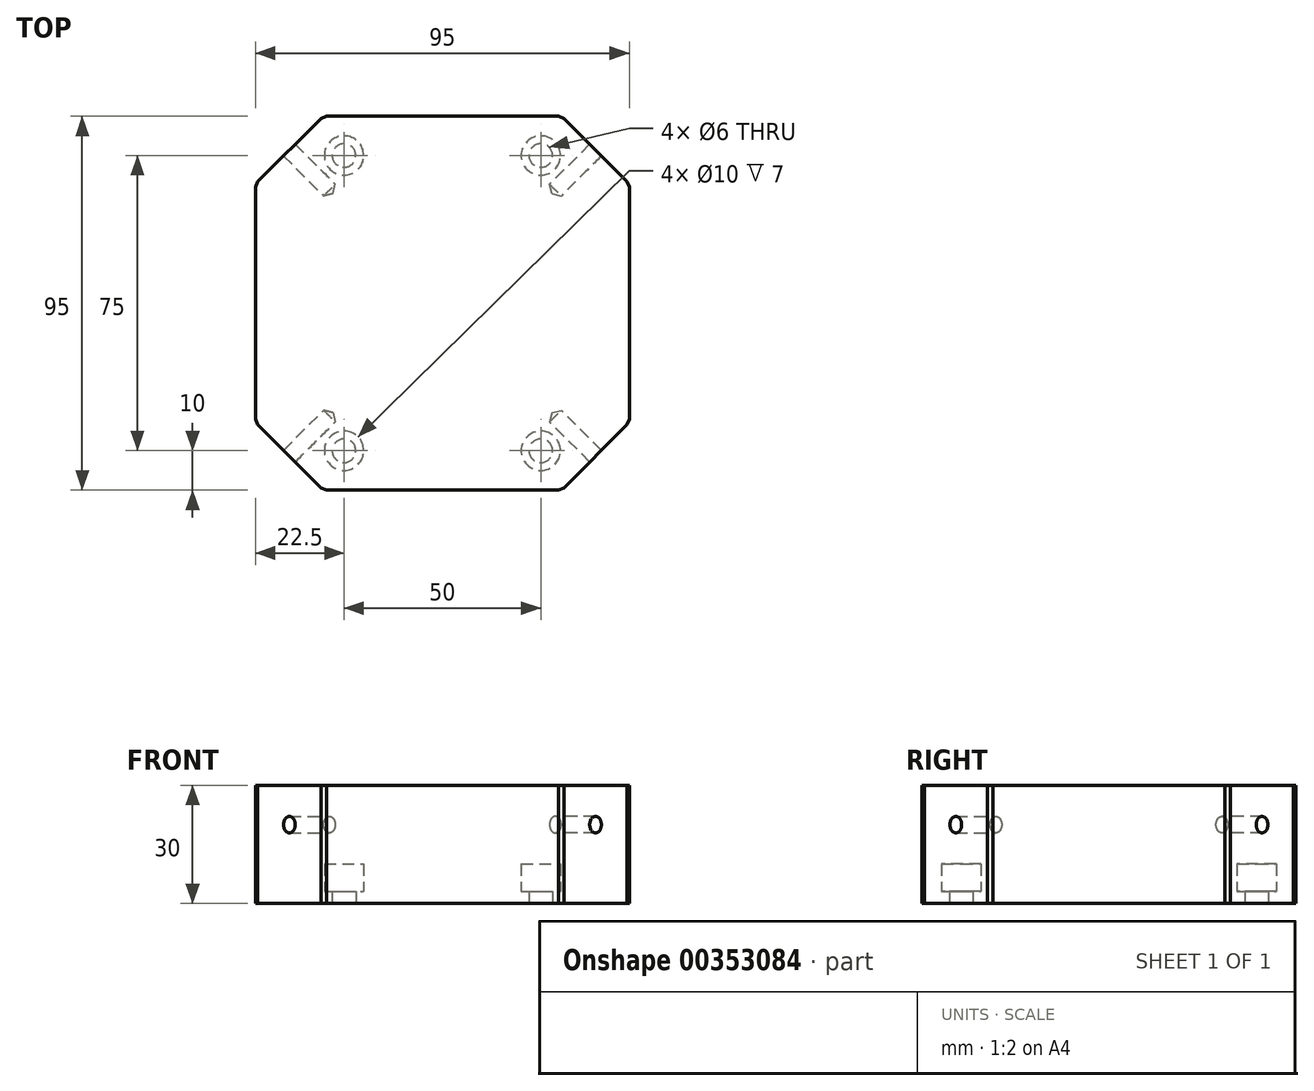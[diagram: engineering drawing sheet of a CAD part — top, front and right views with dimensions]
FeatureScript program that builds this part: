
annotation { "Feature Type Name" : "Feature", "Feature Type Description" : "" }
export const myFeature = defineFeature(function(context is Context, id is Id, definition is map)
    precondition{}
    {
        {
            var Q0;
            Q0=qCreatedBy(makeId("Top.planeOp"),FACE);
            var sketch = newSketch(context, id + "F0", { "sketchPlane" : qUnion([Q0])});
            skLineSegment(sketch, "E0.bottom", {"start": v(-47.5, 47.5) * mm, "end": v(47.5, 47.5) * mm});
            skLineSegment(sketch, "E0.top", {"start": v(-47.5, -47.5) * mm, "end": v(47.5, -47.5) * mm});
            skLineSegment(sketch, "E0.left", {"start": v(-47.5, 47.5) * mm, "end": v(-47.5, -47.5) * mm});
            skLineSegment(sketch, "E0.right", {"start": v(47.5, 47.5) * mm, "end": v(47.5, -47.5) * mm});
            skCircle(sketch, "E1", {"center": v(0, 0) * mm, "radius": 50.15 * mm});
            skPoint(sketch, "E2", {"position": v(-25, 37.5) * mm});
            skPoint(sketch, "E3.MirrorP", {"position": v(25, 37.5) * mm});
            skPoint(sketch, "E4.MirrorP", {"position": v(-25, -37.5) * mm});
            skPoint(sketch, "E5.MirrorP", {"position": v(25, -37.5) * mm});
            skLineSegment(sketch, "E6.bottom", {"start": v(77.78, 0) * mm, "end": v(0, -77.78) * mm});
            skLineSegment(sketch, "E6.top", {"start": v(0, 77.78) * mm, "end": v(-77.78, 0) * mm});
            skLineSegment(sketch, "E6.left", {"start": v(77.78, 0) * mm, "end": v(0, 77.78) * mm});
            skLineSegment(sketch, "E6.right", {"start": v(0, -77.78) * mm, "end": v(-77.78, 0) * mm});
            skSolve(sketch);
        }
        {
            var Q0;
            {var subQ0=sQuery(id+"F0.wireOp",EDGE,"E1");var subQ10=sQuery(id+"F0.wireOp",EDGE,"E0.bottom");var subQ11=makeQuery(id+"F0.imprint","INTERSECT",VERTEX,{"disambiguationData":[OD(0.0)],"derivedFrom":[subQ10,subQ0]});Q0=makeQuery(id+"F0.imprint","IMPRINT",FACE,{"disambiguationData":[TD([[makeQuery(id+"F0.imprint","IMPRINT",EDGE,{"disambiguationData":[TD([[subQ11,-1.0]])],"derivedFrom":subQ10}),-1.0]])]});}
            var Q1;
            {var subQ0=sQuery(id+"F0.wireOp",EDGE,"XF65z8Od-p8Gt-gOkY-70P6-u7OeU0bEHKry");var subQ1=sQuery(id+"F0.wireOp",EDGE,"E0.bottom");var subQ2=makeQuery(id+"F0.imprint","INTERSECT",VERTEX,{"disambiguationData":[OD(0.0)],"derivedFrom":[subQ1,subQ0]});Q1=makeQuery(id+"F0.imprint","IMPRINT",FACE,{"disambiguationData":[TD([[makeQuery(id+"F0.imprint","IMPRINT",EDGE,{"disambiguationData":[TD([[subQ2,-1.0]])],"derivedFrom":subQ1}),-1.0]])]});}
            var Q2;
            {var subQ0=sQuery(id+"F0.wireOp",EDGE,"XF65z8Od-p8Gt-gOkY-70P6-u7OeU0bEHKry");var subQ1=sQuery(id+"F0.wireOp",EDGE,"E0.top");var subQ2=makeQuery(id+"F0.imprint","INTERSECT",VERTEX,{"disambiguationData":[OD(0.0)],"derivedFrom":[subQ1,subQ0]});Q2=makeQuery(id+"F0.imprint","IMPRINT",FACE,{"disambiguationData":[TD([[makeQuery(id+"F0.imprint","IMPRINT",EDGE,{"disambiguationData":[TD([[subQ2,-1.0]])],"derivedFrom":subQ1}),1.0]])]});}
            var Q3;
            {var subQ0=sQuery(id+"F0.wireOp",EDGE,"XF65z8Od-p8Gt-gOkY-70P6-u7OeU0bEHKry");var subQ1=sQuery(id+"F0.wireOp",EDGE,"E0.top");var subQ2=makeQuery(id+"F0.imprint","INTERSECT",VERTEX,{"disambiguationData":[OD(1.0)],"derivedFrom":[subQ1,subQ0]});Q3=makeQuery(id+"F0.imprint","IMPRINT",FACE,{"disambiguationData":[TD([[makeQuery(id+"F0.imprint","IMPRINT",EDGE,{"disambiguationData":[TD([[subQ2,1.0]])],"derivedFrom":subQ1}),1.0]])]});}
            var Q4;
            {var subQ0=sQuery(id+"F0.wireOp",EDGE,"XF65z8Od-p8Gt-gOkY-70P6-u7OeU0bEHKry");var subQ1=sQuery(id+"F0.wireOp",EDGE,"E0.bottom");var subQ2=makeQuery(id+"F0.imprint","INTERSECT",VERTEX,{"disambiguationData":[OD(1.0)],"derivedFrom":[subQ1,subQ0]});Q4=makeQuery(id+"F0.imprint","IMPRINT",FACE,{"disambiguationData":[TD([[makeQuery(id+"F0.imprint","IMPRINT",EDGE,{"disambiguationData":[TD([[subQ2,1.0]])],"derivedFrom":subQ1}),-1.0]])]});}
            var Q5;
            {var subQ0=sQuery(id+"F0.wireOp",EDGE,"E6.right");var subQ1=sQuery(id+"F0.wireOp",EDGE,"E0.top");var subQ2=makeQuery(id+"F0.imprint","INTERSECT",VERTEX,{"derivedFrom":[subQ1,subQ0]});Q5=makeQuery(id+"F0.imprint","IMPRINT",FACE,{"disambiguationData":[TD([[makeQuery(id+"F0.imprint","IMPRINT",EDGE,{"disambiguationData":[TD([[subQ2,-1.0]])],"derivedFrom":subQ1}),1.0]])]});}
            var Q6;
            {var subQ0=sQuery(id+"F0.wireOp",EDGE,"E6.top");var subQ1=sQuery(id+"F0.wireOp",EDGE,"E0.bottom");var subQ2=makeQuery(id+"F0.imprint","INTERSECT",VERTEX,{"derivedFrom":[subQ1,subQ0]});Q6=makeQuery(id+"F0.imprint","IMPRINT",FACE,{"disambiguationData":[TD([[makeQuery(id+"F0.imprint","IMPRINT",EDGE,{"disambiguationData":[TD([[subQ2,-1.0]])],"derivedFrom":subQ1}),-1.0]])]});}
            var Q7;
            {var subQ0=sQuery(id+"F0.wireOp",EDGE,"E6.left");var subQ1=sQuery(id+"F0.wireOp",EDGE,"E0.bottom");var subQ2=makeQuery(id+"F0.imprint","INTERSECT",VERTEX,{"derivedFrom":[subQ1,subQ0]});Q7=makeQuery(id+"F0.imprint","IMPRINT",FACE,{"disambiguationData":[TD([[makeQuery(id+"F0.imprint","IMPRINT",EDGE,{"disambiguationData":[TD([[subQ2,1.0]])],"derivedFrom":subQ1}),-1.0]])]});}
            var Q8;
            {var subQ0=sQuery(id+"F0.wireOp",EDGE,"E6.bottom");var subQ1=sQuery(id+"F0.wireOp",EDGE,"E0.top");var subQ2=makeQuery(id+"F0.imprint","INTERSECT",VERTEX,{"derivedFrom":[subQ1,subQ0]});Q8=makeQuery(id+"F0.imprint","IMPRINT",FACE,{"disambiguationData":[TD([[makeQuery(id+"F0.imprint","IMPRINT",EDGE,{"disambiguationData":[TD([[subQ2,1.0]])],"derivedFrom":subQ1}),1.0]])]});}
            var Q9;
            Q9=sQuery(id+"F0.wireOp",EDGE,"E0.right");
            var Q10;
            Q10=sQuery(id+"F0.wireOp",EDGE,"E0.bottom");
            var Q11;
            Q11=sQuery(id+"F0.wireOp",EDGE,"E0.left");
            var Q12;
            Q12=sQuery(id+"F0.wireOp",EDGE,"E0.top");
            extrude(context, id + "F1", {"entities" : qUnion([Q0, Q1, Q2, Q3, Q4, Q5, Q6, Q7, Q8]), "flatOperationType" : FlatOperationType.REMOVE, "surfaceEntities" : qUnion([Q9, Q10, Q11, Q12]), "offsetDistance" : 25 * mm, "depth" : 0 * mm, "hasSecondDirection" : true, "secondDirectionOppositeDirection" : true, "secondDirectionDepth" : 10 * mm, "domain" : OperationDomain.MODEL});
        }
        {
            var Q0;
            {var subQ0=sQuery(id+"F0.wireOp",EDGE,"XF65z8Od-p8Gt-gOkY-70P6-u7OeU0bEHKry");var subQ1=sQuery(id+"F0.wireOp",EDGE,"E0.bottom");var subQ2=makeQuery(id+"F0.imprint","INTERSECT",VERTEX,{"disambiguationData":[OD(0.0)],"derivedFrom":[subQ1,subQ0]});Q0=makeQuery(id+"F0.imprint","IMPRINT",FACE,{"disambiguationData":[TD([[makeQuery(id+"F0.imprint","IMPRINT",EDGE,{"disambiguationData":[TD([[subQ2,-1.0]])],"derivedFrom":subQ1}),-1.0]])]});}
            var Q1;
            {var subQ0=sQuery(id+"F0.wireOp",EDGE,"XF65z8Od-p8Gt-gOkY-70P6-u7OeU0bEHKry");var subQ1=sQuery(id+"F0.wireOp",EDGE,"E0.bottom");var subQ2=makeQuery(id+"F0.imprint","INTERSECT",VERTEX,{"disambiguationData":[OD(1.0)],"derivedFrom":[subQ1,subQ0]});Q1=makeQuery(id+"F0.imprint","IMPRINT",FACE,{"disambiguationData":[TD([[makeQuery(id+"F0.imprint","IMPRINT",EDGE,{"disambiguationData":[TD([[subQ2,1.0]])],"derivedFrom":subQ1}),-1.0]])]});}
            var Q2;
            {var subQ0=sQuery(id+"F0.wireOp",EDGE,"XF65z8Od-p8Gt-gOkY-70P6-u7OeU0bEHKry");var subQ1=sQuery(id+"F0.wireOp",EDGE,"E0.top");var subQ2=makeQuery(id+"F0.imprint","INTERSECT",VERTEX,{"disambiguationData":[OD(1.0)],"derivedFrom":[subQ1,subQ0]});Q2=makeQuery(id+"F0.imprint","IMPRINT",FACE,{"disambiguationData":[TD([[makeQuery(id+"F0.imprint","IMPRINT",EDGE,{"disambiguationData":[TD([[subQ2,1.0]])],"derivedFrom":subQ1}),1.0]])]});}
            var Q3;
            {var subQ0=sQuery(id+"F0.wireOp",EDGE,"XF65z8Od-p8Gt-gOkY-70P6-u7OeU0bEHKry");var subQ1=sQuery(id+"F0.wireOp",EDGE,"E0.top");var subQ2=makeQuery(id+"F0.imprint","INTERSECT",VERTEX,{"disambiguationData":[OD(0.0)],"derivedFrom":[subQ1,subQ0]});Q3=makeQuery(id+"F0.imprint","IMPRINT",FACE,{"disambiguationData":[TD([[makeQuery(id+"F0.imprint","IMPRINT",EDGE,{"disambiguationData":[TD([[subQ2,-1.0]])],"derivedFrom":subQ1}),1.0]])]});}
            var Q4;
            {var subQ0=sQuery(id+"F0.wireOp",EDGE,"E6.right");var subQ1=sQuery(id+"F0.wireOp",EDGE,"E0.top");var subQ2=makeQuery(id+"F0.imprint","INTERSECT",VERTEX,{"derivedFrom":[subQ1,subQ0]});Q4=makeQuery(id+"F0.imprint","IMPRINT",FACE,{"disambiguationData":[TD([[makeQuery(id+"F0.imprint","IMPRINT",EDGE,{"disambiguationData":[TD([[subQ2,-1.0]])],"derivedFrom":subQ1}),1.0]])]});}
            var Q5;
            {var subQ0=sQuery(id+"F0.wireOp",EDGE,"E6.top");var subQ1=sQuery(id+"F0.wireOp",EDGE,"E0.bottom");var subQ2=makeQuery(id+"F0.imprint","INTERSECT",VERTEX,{"derivedFrom":[subQ1,subQ0]});Q5=makeQuery(id+"F0.imprint","IMPRINT",FACE,{"disambiguationData":[TD([[makeQuery(id+"F0.imprint","IMPRINT",EDGE,{"disambiguationData":[TD([[subQ2,-1.0]])],"derivedFrom":subQ1}),-1.0]])]});}
            var Q6;
            {var subQ0=sQuery(id+"F0.wireOp",EDGE,"E6.left");var subQ1=sQuery(id+"F0.wireOp",EDGE,"E0.bottom");var subQ2=makeQuery(id+"F0.imprint","INTERSECT",VERTEX,{"derivedFrom":[subQ1,subQ0]});Q6=makeQuery(id+"F0.imprint","IMPRINT",FACE,{"disambiguationData":[TD([[makeQuery(id+"F0.imprint","IMPRINT",EDGE,{"disambiguationData":[TD([[subQ2,1.0]])],"derivedFrom":subQ1}),-1.0]])]});}
            var Q7;
            {var subQ0=sQuery(id+"F0.wireOp",EDGE,"E6.bottom");var subQ1=sQuery(id+"F0.wireOp",EDGE,"E0.top");var subQ2=makeQuery(id+"F0.imprint","INTERSECT",VERTEX,{"derivedFrom":[subQ1,subQ0]});Q7=makeQuery(id+"F0.imprint","IMPRINT",FACE,{"disambiguationData":[TD([[makeQuery(id+"F0.imprint","IMPRINT",EDGE,{"disambiguationData":[TD([[subQ2,1.0]])],"derivedFrom":subQ1}),1.0]])]});}
            extrude(context, id + "F2", {"entities" : qUnion([Q0, Q1, Q2, Q3, Q4, Q5, Q6, Q7]), "operationType" : NewBodyOperationType.ADD, "flatOperationType" : FlatOperationType.REMOVE, "offsetDistance" : 25 * mm, "depth" : 20 * mm, "domain" : OperationDomain.MODEL});
        }
        {
            var Q0;
            {var subQ0=sQuery(id+"F0.wireOp",EDGE,"E1");var subQ1=sQuery(id+"F0.wireOp",EDGE,"E0.left");Q0=makeQuery(id+"F2.opExtrude","SWEPT_EDGE",EDGE,{"disambiguationData":[OSD([subQ1,subQ0]),TDD([makeQuery(id+"F0.imprint","INTERSECT",VERTEX,{"disambiguationData":[OD(0.0)],"derivedFrom":[subQ1,subQ0]})])]});}
            var Q1;
            {var subQ0=sQuery(id+"F0.wireOp",EDGE,"E1");var subQ1=sQuery(id+"F0.wireOp",EDGE,"E0.left");Q1=makeQuery(id+"F2.opExtrude","SWEPT_EDGE",EDGE,{"disambiguationData":[OSD([subQ1,subQ0]),TDD([makeQuery(id+"F0.imprint","INTERSECT",VERTEX,{"disambiguationData":[OD(1.0)],"derivedFrom":[subQ1,subQ0]})])]});}
            var Q2;
            {var subQ0=sQuery(id+"F0.wireOp",EDGE,"E1");var subQ1=sQuery(id+"F0.wireOp",EDGE,"E0.top");Q2=makeQuery(id+"F2.opExtrude","SWEPT_EDGE",EDGE,{"disambiguationData":[OSD([subQ1,subQ0]),TDD([makeQuery(id+"F0.imprint","INTERSECT",VERTEX,{"disambiguationData":[OD(0.0)],"derivedFrom":[subQ1,subQ0]})])]});}
            var Q3;
            {var subQ0=sQuery(id+"F0.wireOp",EDGE,"E1");var subQ1=sQuery(id+"F0.wireOp",EDGE,"E0.top");Q3=makeQuery(id+"F2.opExtrude","SWEPT_EDGE",EDGE,{"disambiguationData":[OSD([subQ1,subQ0]),TDD([makeQuery(id+"F0.imprint","INTERSECT",VERTEX,{"disambiguationData":[OD(1.0)],"derivedFrom":[subQ1,subQ0]})])]});}
            var Q4;
            {var subQ0=sQuery(id+"F0.wireOp",EDGE,"E1");var subQ1=sQuery(id+"F0.wireOp",EDGE,"E0.right");Q4=makeQuery(id+"F2.opExtrude","SWEPT_EDGE",EDGE,{"disambiguationData":[OSD([subQ1,subQ0]),TDD([makeQuery(id+"F0.imprint","INTERSECT",VERTEX,{"disambiguationData":[OD(1.0)],"derivedFrom":[subQ1,subQ0]})])]});}
            var Q5;
            {var subQ0=sQuery(id+"F0.wireOp",EDGE,"E1");var subQ1=sQuery(id+"F0.wireOp",EDGE,"E0.right");Q5=makeQuery(id+"F2.opExtrude","SWEPT_EDGE",EDGE,{"disambiguationData":[OSD([subQ1,subQ0]),TDD([makeQuery(id+"F0.imprint","INTERSECT",VERTEX,{"disambiguationData":[OD(0.0)],"derivedFrom":[subQ1,subQ0]})])]});}
            var Q6;
            {var subQ0=sQuery(id+"F0.wireOp",EDGE,"E1");var subQ1=sQuery(id+"F0.wireOp",EDGE,"E0.bottom");Q6=makeQuery(id+"F2.opExtrude","SWEPT_EDGE",EDGE,{"disambiguationData":[OSD([subQ1,subQ0]),TDD([makeQuery(id+"F0.imprint","INTERSECT",VERTEX,{"disambiguationData":[OD(1.0)],"derivedFrom":[subQ1,subQ0]})])]});}
            var Q7;
            {var subQ0=sQuery(id+"F0.wireOp",EDGE,"E1");var subQ1=sQuery(id+"F0.wireOp",EDGE,"E0.bottom");Q7=makeQuery(id+"F2.opExtrude","SWEPT_EDGE",EDGE,{"disambiguationData":[OSD([subQ1,subQ0]),TDD([makeQuery(id+"F0.imprint","INTERSECT",VERTEX,{"disambiguationData":[OD(0.0)],"derivedFrom":[subQ1,subQ0]})])]});}
            chamfer(context, id + "F3", {"entities" : qUnion([Q0, Q1, Q2, Q3, Q4, Q5, Q6, Q7]), "width" : 2 * mm, "tangentPropagation" : true});
        }
        {
            var Q0;
            Q0=sQuery(id+"F0.wireOp",VERTEX,"E2");
            var Q1;
            Q1=sQuery(id+"F0.wireOp",VERTEX,"E4.MirrorP");
            var Q2;
            Q2=sQuery(id+"F0.wireOp",VERTEX,"E5.MirrorP");
            var Q3;
            Q3=sQuery(id+"F0.wireOp",VERTEX,"E3.MirrorP");
            var Q4;
            Q4=makeQuery(id+"F1.opExtrude","SWEPT_BODY",BODY,{"disambiguationData":[OSD([sQuery(id+"F0.wireOp",EDGE,"E0.bottom"),sQuery(id+"F0.wireOp",EDGE,"E0.top"),sQuery(id+"F0.wireOp",EDGE,"E0.left"),sQuery(id+"F0.wireOp",EDGE,"E0.right")])]});
            hole(context, id + "F4", {"style" : HoleStyle.C_BORE, "endStyle" : HoleEndStyle.THROUGH, "holeDiameter" : 6 * mm, "cBoreDiameter" : 10 * mm, "cBoreDepth" : 7 * mm, "isTappedThrough" : true, "tappedDepth" : 12 * mm, "tapClearance" : 3, "startFromSketch" : true, "locations" : qUnion([Q0, Q1, Q2, Q3]), "scope" : qUnion([Q4])});
        }
        {
            var Q0;
            {var subQ0=sQuery(id+"F0.wireOp",EDGE,"E6.top");Q0=makeQuery(id+"F2.boolean.opBoolean","MERGE",FACE,{"derivedFrom":[makeQuery(id+"F1.opExtrude","SWEPT_FACE",FACE,{"disambiguationData":[OSD([subQ0])]}),makeQuery(id+"F2.opExtrude","SWEPT_FACE",FACE,{"disambiguationData":[OSD([subQ0])]})]});}
            var sketch = newSketch(context, id + "F5", { "sketchPlane" : qUnion([Q0])});
            skPoint(sketch, "E7", {"position": v(0, 10) * mm});
            skPoint(sketch, "E7.positionSnap0", {"position": v(0, 20) * mm});
            skLineSegment(sketch, "E8", {"start": v(0, 10) * mm, "end": v(0, 20) * mm});
            skSolve(sketch);
        }
        {
            var Q0;
            {var subQ0=sQuery(id+"F0.wireOp",EDGE,"E6.left");Q0=makeQuery(id+"F2.boolean.opBoolean","MERGE",FACE,{"derivedFrom":[makeQuery(id+"F1.opExtrude","SWEPT_FACE",FACE,{"disambiguationData":[OSD([subQ0])]}),makeQuery(id+"F2.opExtrude","SWEPT_FACE",FACE,{"disambiguationData":[OSD([subQ0])]})]});}
            var sketch = newSketch(context, id + "F6", { "sketchPlane" : qUnion([Q0])});
            skLineSegment(sketch, "E9", {"start": v(0, 20) * mm, "end": v(0, 10) * mm});
            skSolve(sketch);
        }
        {
            var Q0;
            {var subQ0=sQuery(id+"F0.wireOp",EDGE,"E6.bottom");Q0=makeQuery(id+"F2.boolean.opBoolean","MERGE",FACE,{"derivedFrom":[makeQuery(id+"F1.opExtrude","SWEPT_FACE",FACE,{"disambiguationData":[OSD([subQ0])]}),makeQuery(id+"F2.opExtrude","SWEPT_FACE",FACE,{"disambiguationData":[OSD([subQ0])]})]});}
            var sketch = newSketch(context, id + "F7", { "sketchPlane" : qUnion([Q0])});
            skLineSegment(sketch, "E10", {"start": v(0, 20) * mm, "end": v(0, 10) * mm});
            skSolve(sketch);
        }
        {
            var Q0;
            {var subQ0=sQuery(id+"F0.wireOp",EDGE,"E6.right");Q0=makeQuery(id+"F2.boolean.opBoolean","MERGE",FACE,{"derivedFrom":[makeQuery(id+"F1.opExtrude","SWEPT_FACE",FACE,{"disambiguationData":[OSD([subQ0])]}),makeQuery(id+"F2.opExtrude","SWEPT_FACE",FACE,{"disambiguationData":[OSD([subQ0])]})]});}
            var sketch = newSketch(context, id + "F8", { "sketchPlane" : qUnion([Q0])});
            skLineSegment(sketch, "E11", {"start": v(0, 20) * mm, "end": v(0, 10) * mm});
            skSolve(sketch);
        }
        {
            var Q0;
            Q0=sQuery(id+"F6.wireOp",VERTEX,"E9.end");
            var Q1;
            Q1=sQuery(id+"F8.wireOp",VERTEX,"E11.end");
            var Q2;
            Q2=sQuery(id+"F5.wireOp",VERTEX,"E8.start");
            var Q3;
            Q3=sQuery(id+"F7.wireOp",VERTEX,"E10.end");
            var Q4;
            Q4=makeQuery(id+"F1.opExtrude","SWEPT_BODY",BODY,{"disambiguationData":[OSD([sQuery(id+"F0.wireOp",EDGE,"E0.bottom"),sQuery(id+"F0.wireOp",EDGE,"E0.top"),sQuery(id+"F0.wireOp",EDGE,"E0.left"),sQuery(id+"F0.wireOp",EDGE,"E0.right"),sQuery(id+"F0.wireOp",EDGE,"E6.bottom"),sQuery(id+"F0.wireOp",EDGE,"E6.top"),sQuery(id+"F0.wireOp",EDGE,"E6.left"),sQuery(id+"F0.wireOp",EDGE,"E6.right")])]});
            hole(context, id + "F9", {"style" : HoleStyle.SIMPLE, "endStyle" : HoleEndStyle.BLIND, "standardTappedOrClearance" : lookupTablePath({ "standard" : "ISO", "engagement" : "75%", "pitch" : "0.8 mm", "size" : "M5", "type" : "Tapped" }), "standardBlindInLast" : lookupTablePath({ "standard" : "ISO", "engagement" : "75%", "pitch" : "0.8 mm", "size" : "M5", "type" : "Tapped" }), "holeDiameter" : 4.2 * mm, "showTappedDepth" : true, "holeDepth" : 14.4 * mm, "isTappedThrough" : true, "tappedDepth" : 12 * mm, "tapClearance" : 3, "startFromSketch" : true, "locations" : qUnion([Q0, Q1, Q2, Q3]), "scope" : qUnion([Q4]), "majorDiameter" : 5 * mm});
        }
    });
